FCSTD DOCUMENT  (FreeCAD 0.14R3637 (Git))
Label: Vexta_motor_adapter
License: CC-BY 3.0
LicenseURL: http://creativecommons.org/licenses/by/3.0/
objects: Sketcher::SketchObject×1
note: 1 computed .brp shape members not serialized (recipe doc carries the construction recipe); baked Part::Feature solids carry a one-line shape summary decoded from their .brp

FEATURE [Sketcher::SketchObject] Sketch
  sketch-geometry (11):
    g0: ArcOfCircle CenterX=0 CenterY=0 CenterZ=0 NormalX=0 NormalY=0 NormalZ=1 Radius=7.5 StartAngle=1.91063 EndAngle=7.51414
    g1: Circle CenterX=15 CenterY=0 CenterZ=0 NormalX=0 NormalY=0 NormalZ=1 Radius=3
    g2: Circle CenterX=-15 CenterY=0 CenterZ=0 NormalX=0 NormalY=0 NormalZ=1 Radius=3
    g3: Circle CenterX=0 CenterY=15 CenterZ=0 NormalX=0 NormalY=0 NormalZ=1 Radius=3
    g4: Circle CenterX=0 CenterY=-15 CenterZ=0 NormalX=0 NormalY=0 NormalZ=1 Radius=3
    g5: LineSegment StartX=-2.5 StartY=4.5 StartZ=0 EndX=2.5 EndY=4.5 EndZ=0
    g6: LineSegment StartX=2.5 StartY=4.5 StartZ=0 EndX=2.5 EndY=7.07107 EndZ=0
    g7: LineSegment [constr] StartX=2.5 StartY=7.07107 StartZ=0 EndX=-2.5 EndY=7.07107 EndZ=0
    g8: LineSegment StartX=-2.5 StartY=7.07107 StartZ=0 EndX=-2.5 EndY=4.5 EndZ=0
    g9: Circle [constr] CenterX=0 CenterY=0 CenterZ=0 NormalX=0 NormalY=0 NormalZ=1 Radius=15
    g10: Circle CenterX=0 CenterY=0 CenterZ=0 NormalX=0 NormalY=0 NormalZ=1 Radius=22.5
  constraints (29):
    c: Coincident(g0,g-1)
    c: PointOnObject(g1,g-1)
    c: PointOnObject(g2,g-1)
    c: PointOnObject(g3,g-2)
    c: PointOnObject(g4,g-2)
    c: Coincident(g5,g6)
    c: Coincident(g8,g5)
    c: Horizontal(g5)
    c: Horizontal(g7)
    c: Vertical(g6)
    c: Vertical(g8)
    c: Equal(g3,g1)
    c: Equal(g1,g2)
    c: Equal(g2,g4)
    c: Symmetric(g3,g4,g-1)
    c: Symmetric(g1,g2,g-2)
    c: Coincident(g9,g-1)
    c: PointOnObject(g3,g9)
    c: PointOnObject(g1,g9)
    c: PointOnObject(g8,g0)
    c: PointOnObject(g7,g0)
    c: Coincident(g10,g-1)
    c: Radius(g0) = 7.5
    c: Radius(g3) = 3
    c: Radius(g9) = 15
    c: Radius(g10) = 22.5
    c: DistanceY(g-1,g5) = 4.5
    c: Coincident(g0,g7)
    c: Coincident(g0,g6)
